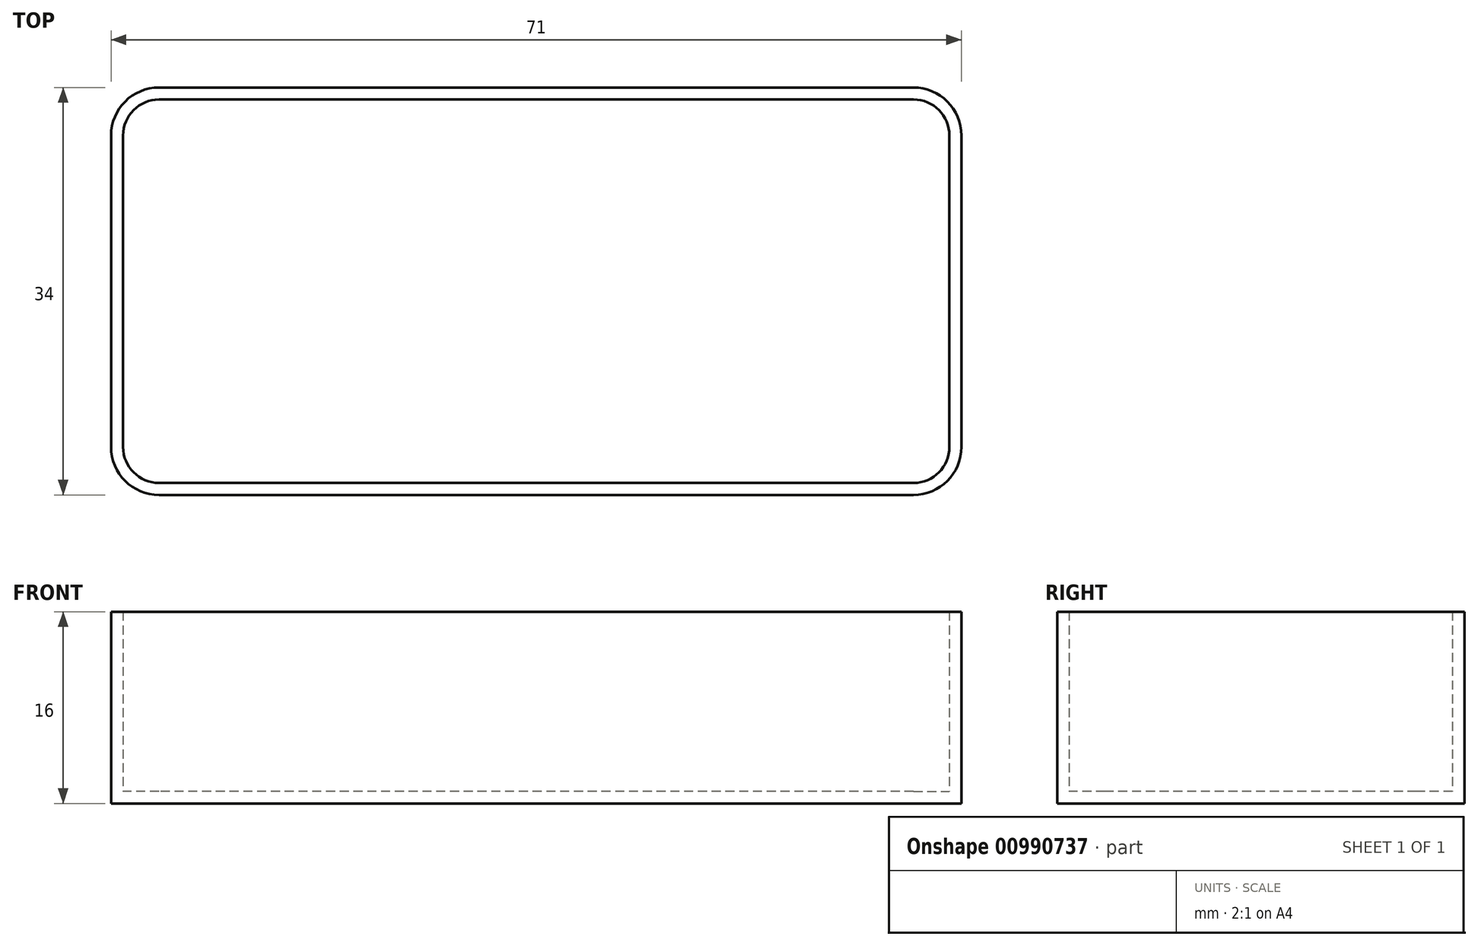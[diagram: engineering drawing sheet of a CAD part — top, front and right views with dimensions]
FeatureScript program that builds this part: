
annotation { "Feature Type Name" : "Feature", "Feature Type Description" : "" }
export const myFeature = defineFeature(function(context is Context, id is Id, definition is map)
    precondition{}
    {
        {
            var Q0;
            Q0=qCreatedBy(makeId("Top.planeOp"),FACE);
            var sketch = newSketch(context, id + "F0", { "sketchPlane" : qUnion([Q0])});
            skLineSegment(sketch, "E0.bottom", {"start": v(30.5, 15) * mm, "end": v(-30.5, 15) * mm});
            skLineSegment(sketch, "E0.top", {"start": v(30.5, -15) * mm, "end": v(-30.5, -15) * mm});
            skLineSegment(sketch, "E0.left", {"start": v(32.5, 13) * mm, "end": v(32.5, 9) * mm});
            skLineSegment(sketch, "E0.right", {"start": v(-32.5, 13) * mm, "end": v(-32.5, -13) * mm});
            skPoint(sketch, "E0.middle", {"position": v(0, 0) * mm});
            skLineSegment(sketch, "E1.bottom", {"start": v(29, 11.5) * mm, "end": v(-29, 11.5) * mm, "construction": true});
            skLineSegment(sketch, "E1.top", {"start": v(29, -11.5) * mm, "end": v(-29, -11.5) * mm, "construction": true});
            skLineSegment(sketch, "E1.left", {"start": v(29, 11.5) * mm, "end": v(29, -11.5) * mm, "construction": true});
            skLineSegment(sketch, "E1.right", {"start": v(-29, 11.5) * mm, "end": v(-29, -11.5) * mm, "construction": true});
            skLineSegment(sketch, "E2.bottom", {"start": v(32.5, -9) * mm, "end": v(34.5, -9) * mm});
            skLineSegment(sketch, "E2.top", {"start": v(32.5, 9) * mm, "end": v(34.5, 9) * mm});
            skLineSegment(sketch, "E2.right", {"start": v(34.5, -9) * mm, "end": v(34.5, 9) * mm});
            skPoint(sketch, "E3", {"position": v(32.5, 0) * mm});
            skLineSegment(sketch, "E4.trimOffspring", {"start": v(32.5, -9) * mm, "end": v(32.5, -13) * mm});
            skCircle(sketch, "E5", {"center": v(-29, 11.5) * mm, "radius": 1.4 * mm});
            skCircle(sketch, "E6", {"center": v(-29, -11.5) * mm, "radius": 1.4 * mm});
            skCircle(sketch, "E7", {"center": v(29, -11.5) * mm, "radius": 1.4 * mm});
            skCircle(sketch, "E8", {"center": v(29, 11.5) * mm, "radius": 1.4 * mm});
            skPoint(sketch, "E9.visualSharp", {"position": v(-32.5, 15) * mm});
            skArc(sketch, "E9.filletArc", {"start": v(-30.5, 15) * mm, "mid": v(-31.91, 14.41) * mm, "end": v(-32.5, 13) * mm});
            skPoint(sketch, "E10.visualSharp", {"position": v(32.5, 15) * mm});
            skArc(sketch, "E10.filletArc", {"start": v(32.5, 13) * mm, "mid": v(31.91, 14.41) * mm, "end": v(30.5, 15) * mm});
            skPoint(sketch, "E11.visualSharp", {"position": v(32.5, -15) * mm});
            skArc(sketch, "E11.filletArc", {"start": v(30.5, -15) * mm, "mid": v(31.91, -14.41) * mm, "end": v(32.5, -13) * mm});
            skPoint(sketch, "E12.visualSharp", {"position": v(-32.5, -15) * mm});
            skArc(sketch, "E12.filletArc", {"start": v(-32.5, -13) * mm, "mid": v(-31.91, -14.41) * mm, "end": v(-30.5, -15) * mm});
            skLineSegment(sketch, "E13", {"start": v(34.5, 9) * mm, "end": v(34.5, 13) * mm, "construction": true});
            skLineSegment(sketch, "E14", {"start": v(32.5, 15) * mm, "end": v(30.5, 15) * mm, "construction": true});
            skLineSegment(sketch, "E15", {"start": v(30.5, -15) * mm, "end": v(32.5, -15) * mm, "construction": true});
            skLineSegment(sketch, "E16", {"start": v(34.5, -15) * mm, "end": v(30.5, -15) * mm, "construction": true});
            skLineSegment(sketch, "E17", {"start": v(34.5, -9) * mm, "end": v(34.5, -13) * mm, "construction": true});
            skPoint(sketch, "E18.visualSharp", {"position": v(34.5, -15) * mm});
            skArc(sketch, "E18.filletArc", {"start": v(32.5, -15) * mm, "mid": v(33.91, -14.41) * mm, "end": v(34.5, -13) * mm, "construction": true});
            skPoint(sketch, "E19.visualSharp", {"position": v(34.5, 15) * mm});
            skArc(sketch, "E19.filletArc", {"start": v(34.5, 13) * mm, "mid": v(33.91, 14.41) * mm, "end": v(32.5, 15) * mm, "construction": true});
            skSolve(sketch);
        }
        {
            var Q0;
            Q0=qCreatedBy(makeId("Top.planeOp"),FACE);
            var sketch = newSketch(context, id + "F1", { "sketchPlane" : qUnion([Q0])});
            skLineSegment(sketch, "E20.0", {"start": v(35.5, -9) * mm, "end": v(35.5, 9) * mm});
            skArc(sketch, "E20.1", {"start": v(-30.5, 16) * mm, "mid": v(-32.62, 15.12) * mm, "end": v(-33.5, 13) * mm});
            skLineSegment(sketch, "E20.2", {"start": v(30.5, 16) * mm, "end": v(-30.5, 16) * mm});
            skLineSegment(sketch, "E20.3", {"start": v(32.5, 16) * mm, "end": v(30.5, 16) * mm});
            skArc(sketch, "E20.4", {"start": v(35.5, 13) * mm, "mid": v(34.62, 15.12) * mm, "end": v(32.5, 16) * mm});
            skLineSegment(sketch, "E20.5", {"start": v(-33.5, 13) * mm, "end": v(-33.5, -13) * mm});
            skLineSegment(sketch, "E20.6", {"start": v(35.5, 9) * mm, "end": v(35.5, 13) * mm});
            skArc(sketch, "E20.7", {"start": v(-33.5, -13) * mm, "mid": v(-32.62, -15.12) * mm, "end": v(-30.5, -16) * mm});
            skLineSegment(sketch, "E20.8", {"start": v(30.5, -16) * mm, "end": v(-30.5, -16) * mm});
            skLineSegment(sketch, "E20.9", {"start": v(30.5, -16) * mm, "end": v(32.5, -16) * mm});
            skArc(sketch, "E20.10", {"start": v(32.5, -16) * mm, "mid": v(34.62, -15.12) * mm, "end": v(35.5, -13) * mm});
            skLineSegment(sketch, "E20.11", {"start": v(35.5, -9) * mm, "end": v(35.5, -13) * mm});
            skSolve(sketch);
        }
        {
            var Q0;
            Q0=makeQuery(id+"F1.imprint","IMPRINT",FACE,{"disambiguationData":[TD([[makeQuery(id+"F1.imprint","IMPRINT",EDGE,{"derivedFrom":sQuery(id+"F1.wireOp",EDGE,"E20.0")}),1.0]])]});
            extrude(context, id + "F2", {"entities" : qUnion([Q0]), "depth" : 15 * mm, "offsetDistance" : 25 * mm});
        }
        {
            var Q0;
            Q0=makeQuery(id+"F2.opExtrude","CAP_FACE",FACE,{"disambiguationData":[OSD([sQuery(id+"F1.wireOp",EDGE,"E20.0"),sQuery(id+"F1.wireOp",EDGE,"E20.1"),sQuery(id+"F1.wireOp",EDGE,"E20.2"),sQuery(id+"F1.wireOp",EDGE,"E20.3"),sQuery(id+"F1.wireOp",EDGE,"E20.4"),sQuery(id+"F1.wireOp",EDGE,"E20.5"),sQuery(id+"F1.wireOp",EDGE,"E20.6"),sQuery(id+"F1.wireOp",EDGE,"E20.7"),sQuery(id+"F1.wireOp",EDGE,"E20.8"),sQuery(id+"F1.wireOp",EDGE,"E20.9"),sQuery(id+"F1.wireOp",EDGE,"E20.10"),sQuery(id+"F1.wireOp",EDGE,"E20.11")])],"isStart":false});
            shell(context, id + "F3", {"entities" : qUnion([Q0]), "thickness" : 1 * mm, "oppositeDirection" : true});
        }
    });
